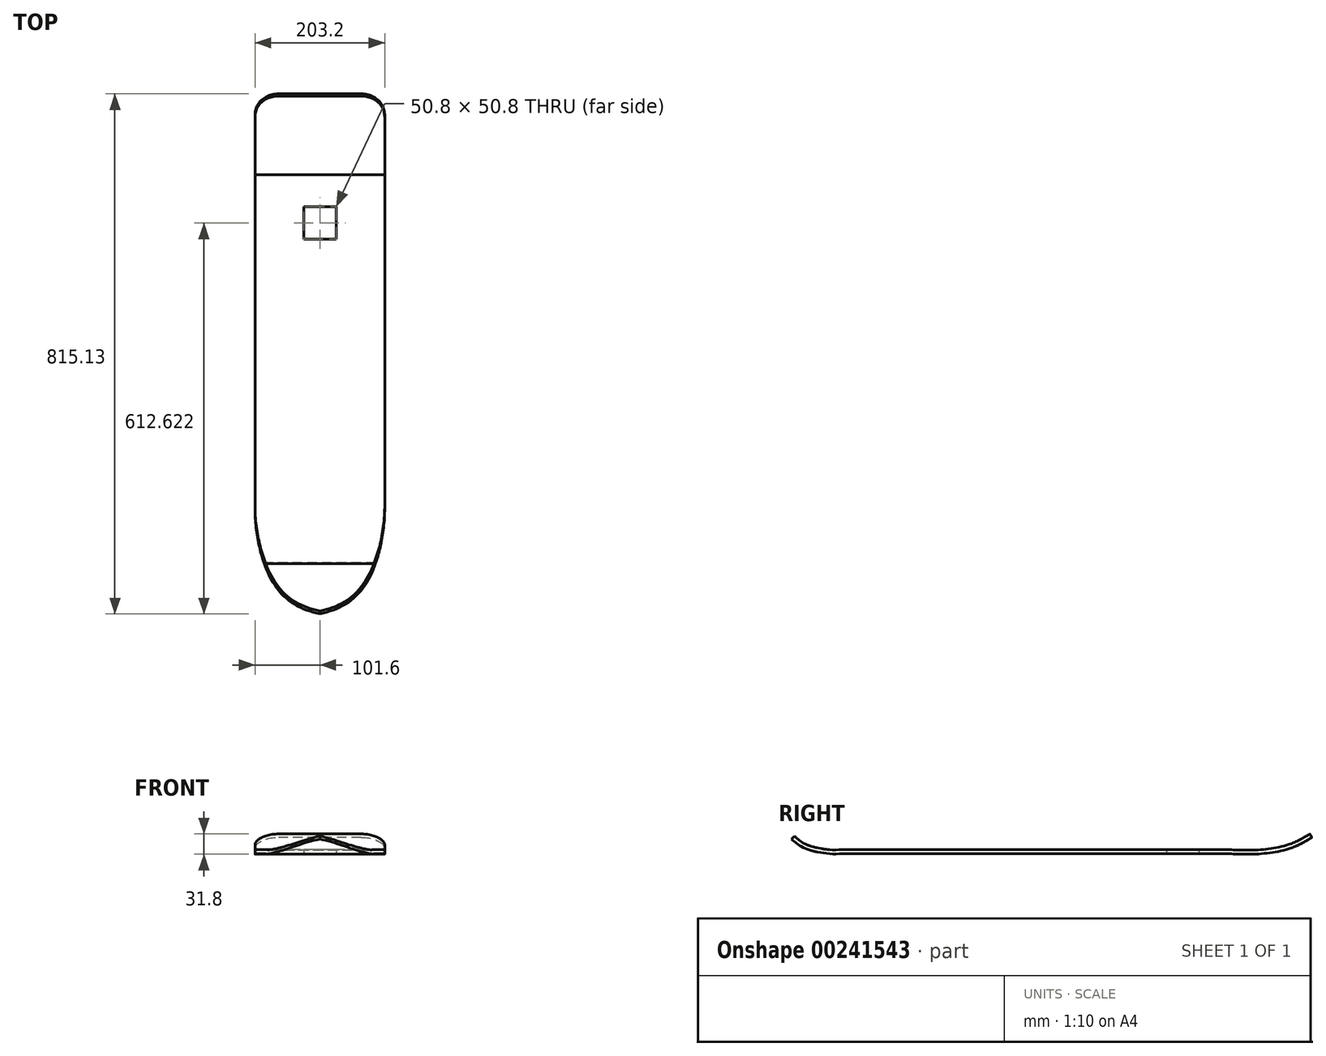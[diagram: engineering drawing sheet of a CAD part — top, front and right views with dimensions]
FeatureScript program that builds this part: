
annotation { "Feature Type Name" : "Feature", "Feature Type Description" : "" }
export const myFeature = defineFeature(function(context is Context, id is Id, definition is map)
    precondition{}
    {
        {
            var Q0;
            Q0=qCreatedBy(makeId("Top.planeOp"),FACE);
            var sketch = newSketch(context, id + "F0", { "sketchPlane" : qUnion([Q0])});
            skLineSegment(sketch, "E0.bottom", {"start": v(101.6, 304.8) * mm, "end": v(-101.6, 304.8) * mm});
            skLineSegment(sketch, "E0.top", {"start": v(101.6, -304.8) * mm, "end": v(-101.6, -304.8) * mm});
            skLineSegment(sketch, "E0.left", {"start": v(101.6, 304.8) * mm, "end": v(101.6, -304.8) * mm});
            skLineSegment(sketch, "E0.right", {"start": v(-101.6, 304.8) * mm, "end": v(-101.6, -304.8) * mm});
            skPoint(sketch, "E0.middle", {"position": v(0, 0) * mm});
            skLineSegment(sketch, "E1.bottom", {"start": v(25.4, 203.58) * mm, "end": v(-25.4, 203.58) * mm});
            skLineSegment(sketch, "E1.top", {"start": v(25.4, 254.38) * mm, "end": v(-25.4, 254.38) * mm});
            skLineSegment(sketch, "E1.left", {"start": v(25.4, 203.58) * mm, "end": v(25.4, 254.38) * mm});
            skLineSegment(sketch, "E1.right", {"start": v(-25.4, 203.58) * mm, "end": v(-25.4, 254.38) * mm});
            skPoint(sketch, "E1.middle", {"position": v(0, 228.98) * mm});
            skPoint(sketch, "E1.middle.positionSnap0", {"position": v(0, 304.8) * mm});
            skPoint(sketch, "E1.centerSnap0", {"position": v(0, 304.8) * mm});
            skCircle(sketch, "E2", {"center": v(-19.05, 248.03) * mm, "radius": 3.18 * mm});
            skCircle(sketch, "E3", {"center": v(19.05, 248.03) * mm, "radius": 3.18 * mm});
            skCircle(sketch, "E4", {"center": v(-19.05, 209.93) * mm, "radius": 3.18 * mm});
            skCircle(sketch, "E5", {"center": v(19.05, 209.93) * mm, "radius": 3.18 * mm});
            skSolve(sketch);
        }
        {
            var Q0;
            Q0 = qSketchRegion(id + "F0", true);
            extrude(context, id + "F1", {"entities" : qUnion([Q0]), "endBound" : BoundingType.SYMMETRIC, "depth" : 6.35 * mm});
        }
        {
            var Q0;
            Q0=qCreatedBy(makeId("Right.planeOp"),FACE);
            var sketch = newSketch(context, id + "F2", { "sketchPlane" : qUnion([Q0])});
            skFitSpline(sketch, "E6", {"points": [v(305.98, 0) * mm, v(348.97, 0) * mm, v(397.6, 9.08) * mm, v(430.73, 26) * mm], "startDerivative": vector(125.25, -4.56) * mm, "endDerivative": vector(99.2, 60.25) * mm});
            skSolve(sketch);
        }
        {
            var Q0;
            Q0=makeQuery(id+"F1.opExtrude","SWEPT_FACE",FACE,{"disambiguationData":[OSD([sQuery(id+"F0.wireOp",EDGE,"E0.bottom")])]});
            var Q1;
            Q1=sQuery(id+"F2.wireOp",EDGE,"E6");
            sweep(context, id + "F3", {"operationType" : NewBodyOperationType.ADD, "profiles" : qUnion([Q0]), "path" : qUnion([Q1])});
        }
        {
            var Q0;
            Q0=qCreatedBy(makeId("Right.planeOp"),FACE);
            var sketch = newSketch(context, id + "F4", { "sketchPlane" : qUnion([Q0])});
            skFitSpline(sketch, "E7", {"points": [v(-303.88, 0) * mm, v(-311.04, 0) * mm, v(-321.78, 0) * mm, v(-361.15, 8.23) * mm, v(-385.49, 26.13) * mm], "startDerivative": vector(-47.75, 0.6) * mm, "endDerivative": vector(-66.33, 64.8) * mm});
            skSolve(sketch);
        }
        {
            var Q0;
            Q0=makeQuery(id+"F1.opExtrude","SWEPT_FACE",FACE,{"disambiguationData":[OSD([sQuery(id+"F0.wireOp",EDGE,"E0.top")])]});
            var Q1;
            Q1=sQuery(id+"F4.wireOp",EDGE,"E7");
            sweep(context, id + "F5", {"operationType" : NewBodyOperationType.ADD, "profiles" : qUnion([Q0]), "path" : qUnion([Q1])});
        }
        {
            var Q0;
            Q0=makeQuery(id+"F5.opSweep","CAP_EDGE",EDGE,{"disambiguationData":[OSD([sQuery(id+"F0.wireOp",EDGE,"E0.top"),sQuery(id+"F0.wireOp",EDGE,"E0.left"),sQuery(id+"F4.wireOp",VERTEX,"E7.end")])],"isStart":false});
            var Q1;
            Q1=makeQuery(id+"F5.opSweep","CAP_EDGE",EDGE,{"disambiguationData":[OSD([sQuery(id+"F0.wireOp",EDGE,"E0.top"),sQuery(id+"F0.wireOp",EDGE,"E0.right"),sQuery(id+"F4.wireOp",VERTEX,"E7.end")])],"isStart":false});
            fillet(context, id + "F6", {"entities" : qUnion([Q0, Q1]), "radius" : 141.04 * mm, "tangentPropagation" : true, "allowEdgeOverflow" : false});
        }
        {
            var Q0;
            Q0=makeQuery(id+"F3.opSweep","CAP_EDGE",EDGE,{"disambiguationData":[OSD([sQuery(id+"F0.wireOp",EDGE,"E0.bottom"),sQuery(id+"F0.wireOp",EDGE,"E0.left"),sQuery(id+"F2.wireOp",VERTEX,"E6.end")])],"isStart":false});
            var Q1;
            Q1=makeQuery(id+"F3.opSweep","CAP_EDGE",EDGE,{"disambiguationData":[OSD([sQuery(id+"F0.wireOp",EDGE,"E0.bottom"),sQuery(id+"F0.wireOp",EDGE,"E0.right"),sQuery(id+"F2.wireOp",VERTEX,"E6.end")])],"isStart":false});
            fillet(context, id + "F7", {"entities" : qUnion([Q0, Q1]), "radius" : 36.8 * mm, "tangentPropagation" : true, "allowEdgeOverflow" : false});
        }
    });
